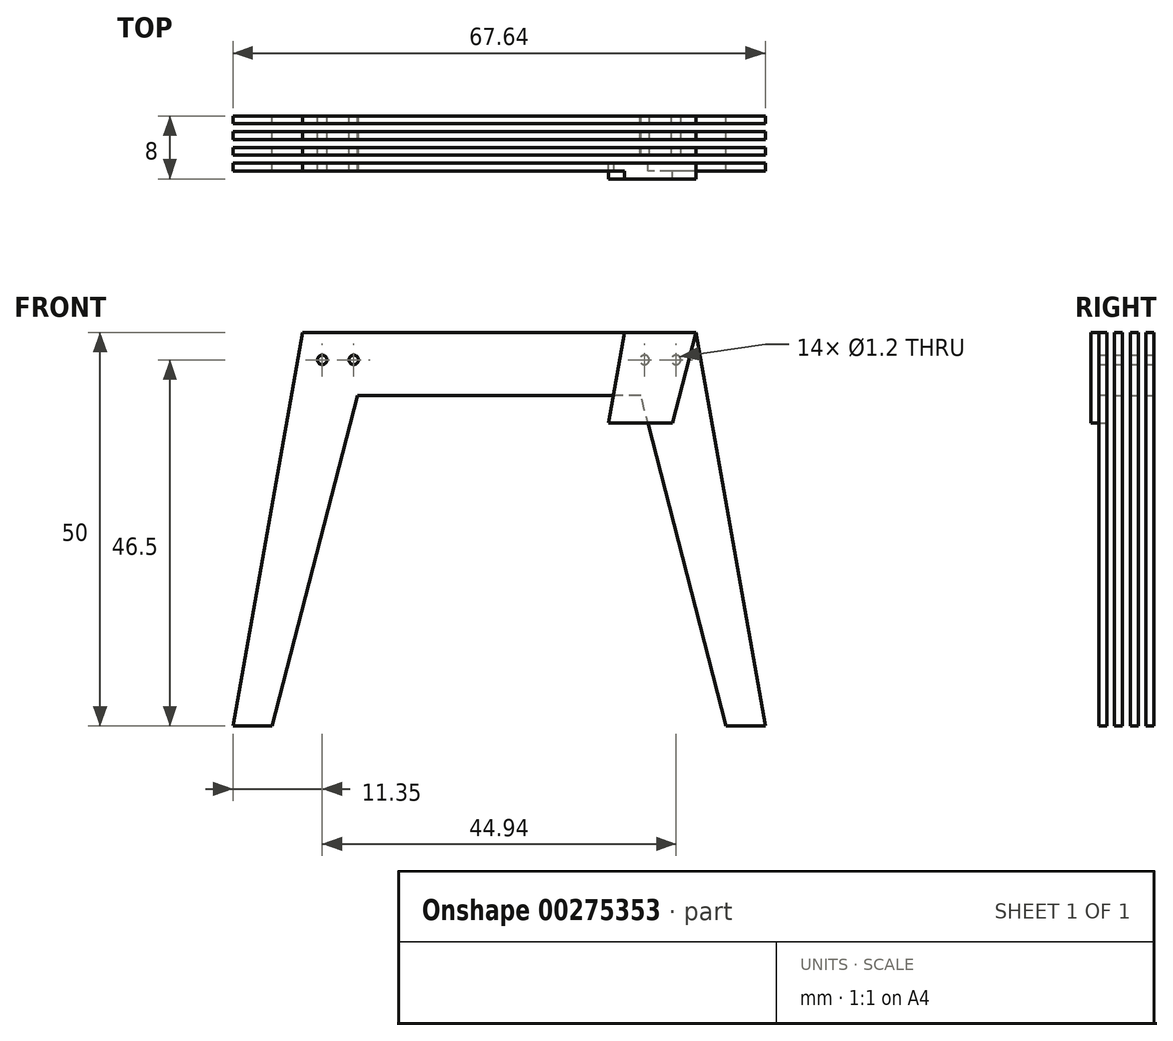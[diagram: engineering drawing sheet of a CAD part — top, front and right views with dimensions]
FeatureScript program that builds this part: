
annotation { "Feature Type Name" : "Feature", "Feature Type Description" : "" }
export const myFeature = defineFeature(function(context is Context, id is Id, definition is map)
    precondition{}
    {
        {
            assignVariable(context, id + "F0", {"name" : "ES", "anyValue" : 1});
        }
        {
            var Q0;
            Q0=qCreatedBy(makeId("Front.planeOp"),FACE);
            var sketch = newSketch(context, id + "F1", { "sketchPlane" : qUnion([Q0])});
            skLineSegment(sketch, "E0", {"start": v(25, 0) * mm, "end": v(33.82, -50) * mm});
            skLineSegment(sketch, "E1", {"start": v(33.82, -50) * mm, "end": v(28.82, -50) * mm});
            skLineSegment(sketch, "E2", {"start": v(28.82, -50) * mm, "end": v(18, -8) * mm});
            skPoint(sketch, "E3", {"position": v(0, -8) * mm});
            skLineSegment(sketch, "E4", {"start": v(18, -8) * mm, "end": v(0, -8) * mm});
            skLineSegment(sketch, "E5", {"start": v(25, 0) * mm, "end": v(15.94, 0) * mm});
            skLineSegment(sketch, "E6", {"start": v(0, 0) * mm, "end": v(0, -8) * mm, "construction": true});
            skLineSegment(sketch, "E7.MirrorCS", {"start": v(-28.82, -50) * mm, "end": v(-18, -8) * mm});
            skLineSegment(sketch, "E8.MirrorCS", {"start": v(-18, -8) * mm, "end": v(0, -8) * mm});
            skLineSegment(sketch, "E9.MirrorCS", {"start": v(-25, 0) * mm, "end": v(0, 0) * mm});
            skLineSegment(sketch, "E10.MirrorCS", {"start": v(-25, 0) * mm, "end": v(-33.82, -50) * mm});
            skLineSegment(sketch, "E11.MirrorCS", {"start": v(-33.82, -50) * mm, "end": v(-28.82, -50) * mm});
            skCircle(sketch, "E12", {"center": v(18.47, -3.5) * mm, "radius": 0.6 * mm});
            skLineSegment(sketch, "E13", {"start": v(20.47, 0) * mm, "end": v(20.47, -8) * mm, "construction": true});
            skPoint(sketch, "E14", {"position": v(20.47, -3.5) * mm});
            skLineSegment(sketch, "E15", {"start": v(18.47, -3.5) * mm, "end": v(20.47, -3.5) * mm, "construction": true});
            skCircle(sketch, "E16.MirrorC", {"center": v(22.47, -3.5) * mm, "radius": 0.6 * mm});
            skCircle(sketch, "E17.MirrorC", {"center": v(-18.47, -3.5) * mm, "radius": 0.6 * mm});
            skCircle(sketch, "E18.MirrorC", {"center": v(-22.47, -3.5) * mm, "radius": 0.6 * mm});
            skLineSegment(sketch, "E19", {"start": v(18, -8) * mm, "end": v(15.94, 0) * mm, "construction": true});
            skLineSegment(sketch, "E20", {"start": v(0, 0) * mm, "end": v(15.94, 0) * mm});
            skSolve(sketch);
        }
        {
            var Q0;
            Q0=makeQuery(id+"F1.imprint","IMPRINT",FACE,{"disambiguationData":[TD([[makeQuery(id+"F1.imprint","IMPRINT",EDGE,{"derivedFrom":sQuery(id+"F1.wireOp",EDGE,"E0")}),-1.0]])]});
            extrude(context, id + "F2", {"entities" : qUnion([Q0]), "depth" : (getVariable(context, 'ES')) * mm, "offsetDistance" : 25 * mm});
        }
        {
            var Q0;
            Q0=makeQuery(id+"F2.opExtrude","SWEPT_BODY",BODY,{"disambiguationData":[OSD([sQuery(id+"F1.wireOp",EDGE,"cBsLhSvx-4s7H-fw2r-Ok7d-ymyCPxTKZssG"),sQuery(id+"F1.wireOp",EDGE,"0nN1IqKL-NWWj-bxm0-EVVQ-cEPFi81hgprU"),sQuery(id+"F1.wireOp",EDGE,"E0"),sQuery(id+"F1.wireOp",EDGE,"E1"),sQuery(id+"F1.wireOp",EDGE,"E2"),sQuery(id+"F1.wireOp",EDGE,"BBcGjcCq-dRdF-kIBx-dHHX-Tyc7wJy0wU36"),sQuery(id+"F1.wireOp",EDGE,"mv5w1zmy-oU2K-3Z8i-JM2j-gp76FdoEEjhY"),sQuery(id+"F1.wireOp",EDGE,"vXSenvXC-5Uvq-79zk-geeN-Bi3KB7lza4Ty"),sQuery(id+"F1.wireOp",EDGE,"6Hz0f7GS-8nOk-5bK6-D4vu-FLWrWiSsHDG4"),sQuery(id+"F1.wireOp",EDGE,"FHWcBbI0-Jken-KiuB-CpeC-YBuBScj9jTTL"),sQuery(id+"F1.wireOp",EDGE,"JAlEa9IU-I5bQ-abA7-rz7y-jNYQNbp1e5kc"),sQuery(id+"F1.wireOp",EDGE,"a64fd290-64e6-4719-af62-52c859a0f731.filletArc"),sQuery(id+"F1.wireOp",EDGE,"e1cd9687-b0e0-4c81-96b5-d1ad45408f12.filletArc"),sQuery(id+"F1.wireOp",EDGE,"9bb30c22-e7d3-4294-b6d6-ea4ecebd2938.filletArc"),sQuery(id+"F1.wireOp",EDGE,"efeb0405-145a-46bc-88a0-e1937dd5107a.filletArc"),sQuery(id+"F1.wireOp",EDGE,"931285cf-8f08-4533-8e18-9d663b5e5b4d.filletArc"),sQuery(id+"F1.wireOp",EDGE,"790d867b-276d-40c0-ad24-b3f3fe030b49.filletArc")])]});
            transform(context, id + "F3", {"entities" : qUnion([Q0]), "transformType" : TransformType.TRANSLATION_3D, "dx" : 0 * mm, "dy" : (getVariable(context, 'ES') * 2) * mm, "dz" : 0 * mm, "makeCopy" : true});
        }
        {
            var Q0;
            Q0=makeQuery(id+"F3.opPattern","COPY",BODY,{"derivedFrom":makeQuery(id+"F2.opExtrude","SWEPT_BODY",BODY,{"disambiguationData":[OSD([sQuery(id+"F1.wireOp",EDGE,"cBsLhSvx-4s7H-fw2r-Ok7d-ymyCPxTKZssG"),sQuery(id+"F1.wireOp",EDGE,"0nN1IqKL-NWWj-bxm0-EVVQ-cEPFi81hgprU"),sQuery(id+"F1.wireOp",EDGE,"E0"),sQuery(id+"F1.wireOp",EDGE,"E1"),sQuery(id+"F1.wireOp",EDGE,"E2"),sQuery(id+"F1.wireOp",EDGE,"BBcGjcCq-dRdF-kIBx-dHHX-Tyc7wJy0wU36"),sQuery(id+"F1.wireOp",EDGE,"mv5w1zmy-oU2K-3Z8i-JM2j-gp76FdoEEjhY"),sQuery(id+"F1.wireOp",EDGE,"vXSenvXC-5Uvq-79zk-geeN-Bi3KB7lza4Ty"),sQuery(id+"F1.wireOp",EDGE,"6Hz0f7GS-8nOk-5bK6-D4vu-FLWrWiSsHDG4"),sQuery(id+"F1.wireOp",EDGE,"FHWcBbI0-Jken-KiuB-CpeC-YBuBScj9jTTL"),sQuery(id+"F1.wireOp",EDGE,"JAlEa9IU-I5bQ-abA7-rz7y-jNYQNbp1e5kc"),sQuery(id+"F1.wireOp",EDGE,"a64fd290-64e6-4719-af62-52c859a0f731.filletArc"),sQuery(id+"F1.wireOp",EDGE,"e1cd9687-b0e0-4c81-96b5-d1ad45408f12.filletArc"),sQuery(id+"F1.wireOp",EDGE,"9bb30c22-e7d3-4294-b6d6-ea4ecebd2938.filletArc"),sQuery(id+"F1.wireOp",EDGE,"efeb0405-145a-46bc-88a0-e1937dd5107a.filletArc"),sQuery(id+"F1.wireOp",EDGE,"931285cf-8f08-4533-8e18-9d663b5e5b4d.filletArc"),sQuery(id+"F1.wireOp",EDGE,"790d867b-276d-40c0-ad24-b3f3fe030b49.filletArc")])]}),"instanceName":"1"});
            transform(context, id + "F4", {"entities" : qUnion([Q0]), "transformType" : TransformType.TRANSLATION_3D, "dx" : 0 * mm, "dy" : (getVariable(context, 'ES') * 2) * mm, "dz" : 0 * mm, "makeCopy" : true});
        }
        {
            var Q0;
            Q0=qCreatedBy(makeId("Front.planeOp"),FACE);
            var sketch = newSketch(context, id + "F5", { "sketchPlane" : qUnion([Q0])});
            skLineSegment(sketch, "E21", {"start": v(25, 0) * mm, "end": v(27.03, -11.5) * mm, "construction": true});
            skLineSegment(sketch, "E22", {"start": v(27.03, -11.5) * mm, "end": v(18.9, -11.5) * mm, "construction": true});
            skLineSegment(sketch, "E23", {"start": v(18.9, -11.5) * mm, "end": v(15.94, 0) * mm, "construction": true});
            skLineSegment(sketch, "E24", {"start": v(25, 0) * mm, "end": v(15.94, 0) * mm, "construction": true});
            skLineSegment(sketch, "E25.MirrorCS", {"start": v(15.94, 0) * mm, "end": v(25, 0) * mm});
            skLineSegment(sketch, "E26.MirrorCS", {"start": v(15.94, 0) * mm, "end": v(13.91, -11.5) * mm});
            skLineSegment(sketch, "E27.MirrorCS", {"start": v(13.91, -11.5) * mm, "end": v(22.04, -11.5) * mm});
            skLineSegment(sketch, "E28.MirrorCS", {"start": v(22.04, -11.5) * mm, "end": v(25, 0) * mm});
            skSolve(sketch);
        }
        {
            var Q0;
            Q0 = qSketchRegion(id + "F5", true);
            extrude(context, id + "F6", {"entities" : qUnion([Q0]), "operationType" : NewBodyOperationType.ADD, "depth" : 2 * mm, "offsetDistance" : 25 * mm});
        }
        {
            var Q0;
            Q0=makeQuery(id+"F4.opPattern","COPY",BODY,{"derivedFrom":makeQuery(id+"F3.opPattern","COPY",BODY,{"derivedFrom":makeQuery(id+"F2.opExtrude","SWEPT_BODY",BODY,{"disambiguationData":[OSD([sQuery(id+"F1.wireOp",EDGE,"E0"),sQuery(id+"F1.wireOp",EDGE,"E1"),sQuery(id+"F1.wireOp",EDGE,"E2"),sQuery(id+"F1.wireOp",EDGE,"E4"),sQuery(id+"F1.wireOp",EDGE,"E5"),sQuery(id+"F1.wireOp",EDGE,"E7.MirrorCS"),sQuery(id+"F1.wireOp",EDGE,"E8.MirrorCS"),sQuery(id+"F1.wireOp",EDGE,"E9.MirrorCS"),sQuery(id+"F1.wireOp",EDGE,"E10.MirrorCS"),sQuery(id+"F1.wireOp",EDGE,"E11.MirrorCS"),sQuery(id+"F1.wireOp",EDGE,"E12"),sQuery(id+"F1.wireOp",EDGE,"E16.MirrorC"),sQuery(id+"F1.wireOp",EDGE,"E17.MirrorC"),sQuery(id+"F1.wireOp",EDGE,"E18.MirrorC")])]}),"instanceName":"1"}),"instanceName":"1"});
            transform(context, id + "F7", {"entities" : qUnion([Q0]), "transformType" : TransformType.TRANSLATION_3D, "dx" : 0 * mm, "dy" : 2 * mm, "dz" : 0 * mm, "makeCopy" : true});
        }
    });
